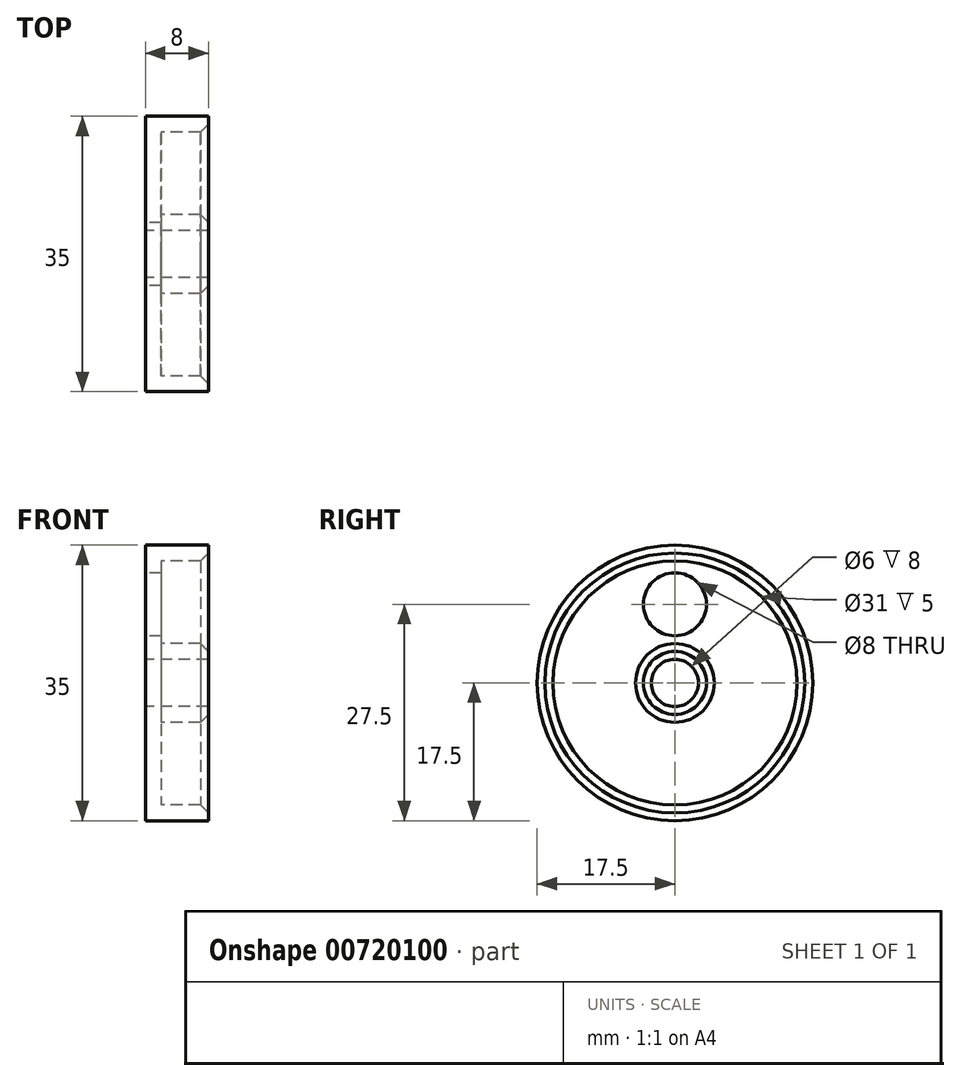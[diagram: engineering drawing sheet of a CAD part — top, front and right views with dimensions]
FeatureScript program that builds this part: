
annotation { "Feature Type Name" : "Feature", "Feature Type Description" : "" }
export const myFeature = defineFeature(function(context is Context, id is Id, definition is map)
    precondition{}
    {
        {
            var Q0;
            Q0=qCreatedBy(makeId("Top.planeOp"),FACE);
            var sketch = newSketch(context, id + "F0", { "sketchPlane" : qUnion([Q0])});
            skLineSegment(sketch, "E0.bottom", {"start": v(0, 0) * mm, "end": v(8, 0) * mm});
            skLineSegment(sketch, "E0.top", {"start": v(0, 17.5) * mm, "end": v(8, 17.5) * mm});
            skLineSegment(sketch, "E0.left", {"start": v(0, 0) * mm, "end": v(0, 17.5) * mm});
            skLineSegment(sketch, "E0.right", {"start": v(8, 0) * mm, "end": v(8, 17.5) * mm});
            skSolve(sketch);
        }
        {
            var Q0;
            Q0 = qSketchRegion(id + "F0", true);
            var Q1;
            Q1=sQuery(id+"F0.wireOp",EDGE,"E0.bottom");
            revolve(context, id + "F1", {"surfaceOperationType" : NewSurfaceOperationType.NEW, "entities" : qUnion([Q0]), "axis" : qUnion([Q1]), "revolveType" : RevolveType.FULL});
        }
        {
            var Q0;
            Q0=qCreatedBy(makeId("Right.planeOp"),FACE);
            var sketch = newSketch(context, id + "F2", { "sketchPlane" : qUnion([Q0])});
            skPoint(sketch, "E1", {"position": v(0, 0) * mm});
            skSolve(sketch);
        }
        {
            var Q0;
            Q0=sQuery(id+"F2.wireOp",VERTEX,"E1");
            var Q1;
            Q1=makeQuery(id+"F1.opRevolve","SWEPT_BODY",BODY,{"disambiguationData":[OSD([sQuery(id+"F0.wireOp",EDGE,"E0.bottom"),sQuery(id+"F0.wireOp",EDGE,"E0.top"),sQuery(id+"F0.wireOp",EDGE,"E0.left"),sQuery(id+"F0.wireOp",EDGE,"E0.right")])]});
            hole(context, id + "F3", {"style" : HoleStyle.SIMPLE, "endStyle" : HoleEndStyle.THROUGH, "oppositeDirection" : true, "holeDiameter" : 6 * mm, "majorDiameter" : 5 * mm, "isTappedThrough" : true, "tappedDepth" : 12 * mm, "tapClearance" : 3, "locations" : qUnion([Q0]), "scope" : qUnion([Q1])});
        }
        {
            var Q0;
            Q0=makeQuery(id+"F1.opRevolve","SWEPT_FACE",FACE,{"disambiguationData":[OSD([sQuery(id+"F0.wireOp",EDGE,"E0.right")])]});
            shell(context, id + "F4", {"entities" : qUnion([Q0]), "thickness" : 2 * mm});
        }
        {
            var Q0;
            Q0=qCreatedBy(makeId("Right.planeOp"),FACE);
            var sketch = newSketch(context, id + "F5", { "sketchPlane" : qUnion([Q0])});
            skPoint(sketch, "E2", {"position": v(0, 10) * mm});
            skSolve(sketch);
        }
        {
            var Q0;
            Q0=sQuery(id+"F5.wireOp",VERTEX,"E2");
            var Q1;
            Q1=makeQuery(id+"F1.opRevolve","SWEPT_BODY",BODY,{"disambiguationData":[OSD([sQuery(id+"F0.wireOp",EDGE,"E0.bottom"),sQuery(id+"F0.wireOp",EDGE,"E0.top"),sQuery(id+"F0.wireOp",EDGE,"E0.left"),sQuery(id+"F0.wireOp",EDGE,"E0.right")])]});
            hole(context, id + "F6", {"style" : HoleStyle.SIMPLE, "endStyle" : HoleEndStyle.THROUGH, "oppositeDirection" : true, "holeDiameter" : 8 * mm, "majorDiameter" : 5 * mm, "isTappedThrough" : true, "tappedDepth" : 12 * mm, "tapClearance" : 3, "locations" : qUnion([Q0]), "scope" : qUnion([Q1])});
        }
        {
            var Q0;
            Q0=makeQuery(id+"F4.opShell","OFFSET_EDGE",EDGE,{"disambiguationData":[OSD([sQuery(id+"F0.wireOp",EDGE,"E0.right"),sQuery(id+"F3.hole-0.sketch.wireOp",EDGE,"core_line_2")])]});
            chamfer(context, id + "F7", {"entities" : qUnion([Q0]), "width" : 1 * mm, "tangentPropagation" : true});
        }
    });
